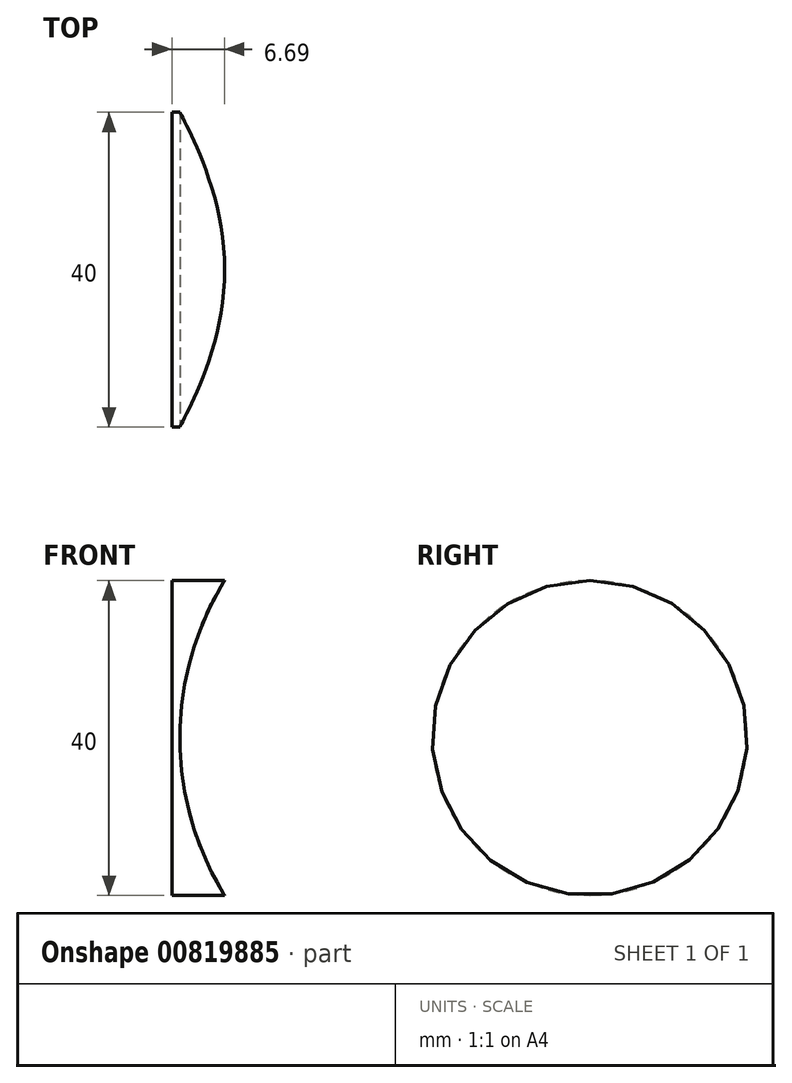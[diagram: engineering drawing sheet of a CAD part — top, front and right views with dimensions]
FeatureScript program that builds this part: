
annotation { "Feature Type Name" : "Feature", "Feature Type Description" : "" }
export const myFeature = defineFeature(function(context is Context, id is Id, definition is map)
    precondition{}
    {
        {
            var Q0;
            Q0=qCreatedBy(makeId("Right.planeOp"),FACE);
            var sketch = newSketch(context, id + "F0", { "sketchPlane" : qUnion([Q0])});
            skCircle(sketch, "E0", {"center": v(0, 0) * mm, "radius": 20 * mm});
            skSolve(sketch);
        }
        {
            var Q0;
            Q0 = qSketchRegion(id + "F0", true);
            extrude(context, id + "F1", {"entities" : qUnion([Q0]), "depth" : 10 * mm, "offsetDistance" : 25 * mm});
        }
        {
            var Q0;
            Q0=qCreatedBy(makeId("Front.planeOp"),FACE);
            var sketch = newSketch(context, id + "F2", { "sketchPlane" : qUnion([Q0])});
            skCircle(sketch, "E1", {"center": v(39, 0) * mm, "radius": 38 * mm});
            skSolve(sketch);
        }
        {
            var Q0;
            Q0 = qSketchRegion(id + "F2", true);
            extrude(context, id + "F3", {"entities" : qUnion([Q0]), "operationType" : NewBodyOperationType.REMOVE, "endBound" : BoundingType.SYMMETRIC, "oppositeDirection" : true, "depth" : 60 * mm, "offsetDistance" : 25 * mm});
        }
    });
